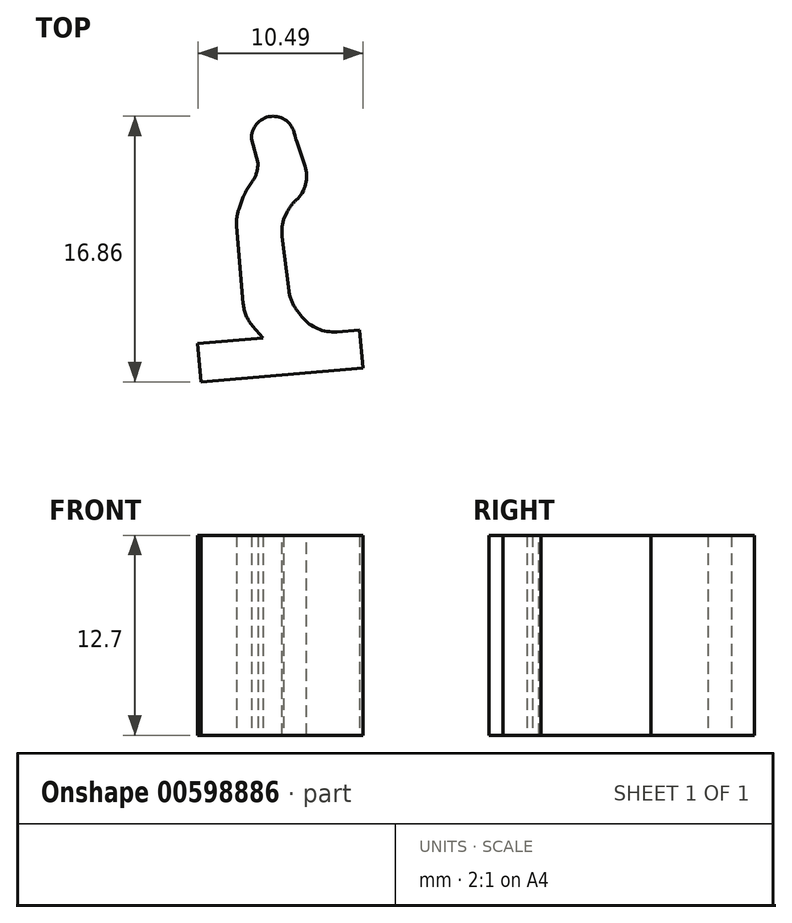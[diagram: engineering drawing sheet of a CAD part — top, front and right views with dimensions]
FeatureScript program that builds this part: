
annotation { "Feature Type Name" : "Feature", "Feature Type Description" : "" }
export const myFeature = defineFeature(function(context is Context, id is Id, definition is map)
    precondition{}
    {
        {
            var Q0;
            Q0=qCreatedBy(makeId("Top.planeOp"),FACE);
            var sketch = newSketch(context, id + "F0", { "sketchPlane" : qUnion([Q0])});
            skLineSegment(sketch, "E0", {"start": v(-20.35, -6.93) * mm, "end": v(-10.07, -6.05) * mm});
            skLineSegment(sketch, "E1", {"start": v(-20.35, -6.93) * mm, "end": v(-20.56, -4.51) * mm});
            skLineSegment(sketch, "E2", {"start": v(-20.56, -4.51) * mm, "end": v(-16.43, -4.16) * mm});
            skLineSegment(sketch, "E3", {"start": v(-16.43, -4.16) * mm, "end": v(-17.6, -2.76) * mm});
            skLineSegment(sketch, "E4", {"start": v(-17.6, -2.76) * mm, "end": v(-18.14, 3.5) * mm});
            skLineSegment(sketch, "E5", {"start": v(-18.14, 3.5) * mm, "end": v(-17.57, 5.08) * mm});
            skLineSegment(sketch, "E6", {"start": v(-17.57, 5.08) * mm, "end": v(-16.74, 6.32) * mm});
            skLineSegment(sketch, "E7", {"start": v(-16.74, 6.32) * mm, "end": v(-16.74, 6.96) * mm});
            skLineSegment(sketch, "E8", {"start": v(-16.74, 6.96) * mm, "end": v(-17.15, 8.47) * mm});
            skLineSegment(sketch, "E9", {"start": v(-14.39, 8.63) * mm, "end": v(-13.41, 5.8) * mm});
            skLineSegment(sketch, "E10", {"start": v(-13.41, 5.8) * mm, "end": v(-13.66, 5.14) * mm});
            skLineSegment(sketch, "E11", {"start": v(-13.66, 5.14) * mm, "end": v(-14.64, 4.35) * mm});
            skLineSegment(sketch, "E12", {"start": v(-14.64, 4.35) * mm, "end": v(-15.13, 3.36) * mm});
            skLineSegment(sketch, "E13", {"start": v(-15.13, 3.36) * mm, "end": v(-15.26, 2.67) * mm});
            skLineSegment(sketch, "E14", {"start": v(-15.26, 2.67) * mm, "end": v(-14.68, -1.88) * mm});
            skLineSegment(sketch, "E15", {"start": v(-14.68, -1.88) * mm, "end": v(-13.08, -3.87) * mm});
            skLineSegment(sketch, "E16", {"start": v(-10.28, -3.63) * mm, "end": v(-10.07, -6.05) * mm});
            skLineSegment(sketch, "E17.trimOffspring", {"start": v(-13.08, -3.87) * mm, "end": v(-10.28, -3.63) * mm});
            skArc(sketch, "E18", {"start": v(-14.39, 8.63) * mm, "mid": v(-15.85, 9.93) * mm, "end": v(-17.15, 8.47) * mm});
            skSolve(sketch);
        }
        {
            var Q0;
            Q0 = qSketchRegion(id + "F0", true);
            extrude(context, id + "F1", {"entities" : qUnion([Q0]), "depth" : 12.7 * mm, "offsetDistance" : 25.4 * mm});
        }
        {
            var Q0;
            Q0=makeQuery(id+"F1.opExtrude","SWEPT_EDGE",EDGE,{"disambiguationData":[OSD([sQuery(id+"F0.wireOp",EDGE,"E9"),sQuery(id+"F0.wireOp",EDGE,"E18")])]});
            var Q1;
            Q1=makeQuery(id+"F1.opExtrude","SWEPT_EDGE",EDGE,{"disambiguationData":[OSD([sQuery(id+"F0.wireOp",EDGE,"E9"),sQuery(id+"F0.wireOp",EDGE,"E10")])]});
            var Q2;
            Q2=makeQuery(id+"F1.opExtrude","SWEPT_EDGE",EDGE,{"disambiguationData":[OSD([sQuery(id+"F0.wireOp",EDGE,"E11"),sQuery(id+"F0.wireOp",EDGE,"E12")])]});
            var Q3;
            Q3=makeQuery(id+"F1.opExtrude","SWEPT_EDGE",EDGE,{"disambiguationData":[OSD([sQuery(id+"F0.wireOp",EDGE,"E13"),sQuery(id+"F0.wireOp",EDGE,"E14")])]});
            var Q4;
            Q4=makeQuery(id+"F1.opExtrude","SWEPT_EDGE",EDGE,{"disambiguationData":[OSD([sQuery(id+"F0.wireOp",EDGE,"E14"),sQuery(id+"F0.wireOp",EDGE,"E15")])]});
            var Q5;
            Q5=makeQuery(id+"F1.opExtrude","SWEPT_EDGE",EDGE,{"disambiguationData":[OSD([sQuery(id+"F0.wireOp",EDGE,"E15"),sQuery(id+"F0.wireOp",EDGE,"E17.trimOffspring")])]});
            var Q6;
            Q6=makeQuery(id+"F1.opExtrude","SWEPT_EDGE",EDGE,{"disambiguationData":[OSD([sQuery(id+"F0.wireOp",EDGE,"E3"),sQuery(id+"F0.wireOp",EDGE,"E4")])]});
            var Q7;
            Q7=makeQuery(id+"F1.opExtrude","SWEPT_EDGE",EDGE,{"disambiguationData":[OSD([sQuery(id+"F0.wireOp",EDGE,"E4"),sQuery(id+"F0.wireOp",EDGE,"E5")])]});
            var Q8;
            Q8=makeQuery(id+"F1.opExtrude","SWEPT_EDGE",EDGE,{"disambiguationData":[OSD([sQuery(id+"F0.wireOp",EDGE,"E5"),sQuery(id+"F0.wireOp",EDGE,"E6")])]});
            fillet(context, id + "F2", {"entities" : qUnion([Q0, Q1, Q2, Q3, Q4, Q5, Q6, Q7, Q8]), "radius" : 2.54 * mm, "tangentPropagation" : true, "allowEdgeOverflow" : false});
        }
        {
            var Q0;
            Q0=makeQuery(id+"F1.opExtrude","SWEPT_EDGE",EDGE,{"disambiguationData":[OSD([sQuery(id+"F0.wireOp",EDGE,"E6"),sQuery(id+"F0.wireOp",EDGE,"E7")])]});
            var Q1;
            Q1=makeQuery(id+"F2.opFillet","BLEND_EDGE",EDGE,{"blendedFrom":[makeQuery(id+"F1.opExtrude","SWEPT_EDGE",EDGE,{"disambiguationData":[OSD([sQuery(id+"F0.wireOp",EDGE,"E9"),sQuery(id+"F0.wireOp",EDGE,"E10")])]}),makeQuery(id+"F1.opExtrude","SWEPT_FACE",FACE,{"disambiguationData":[OSD([sQuery(id+"F0.wireOp",EDGE,"E11")])]})],"blendedInto":[makeQuery(id+"F1.opExtrude","SWEPT_FACE",FACE,{"disambiguationData":[OSD([sQuery(id+"F0.wireOp",EDGE,"E11")])]})]});
            fillet(context, id + "F3", {"entities" : qUnion([Q0, Q1]), "radius" : 2.03 * mm, "tangentPropagation" : true, "allowEdgeOverflow" : false});
        }
    });
